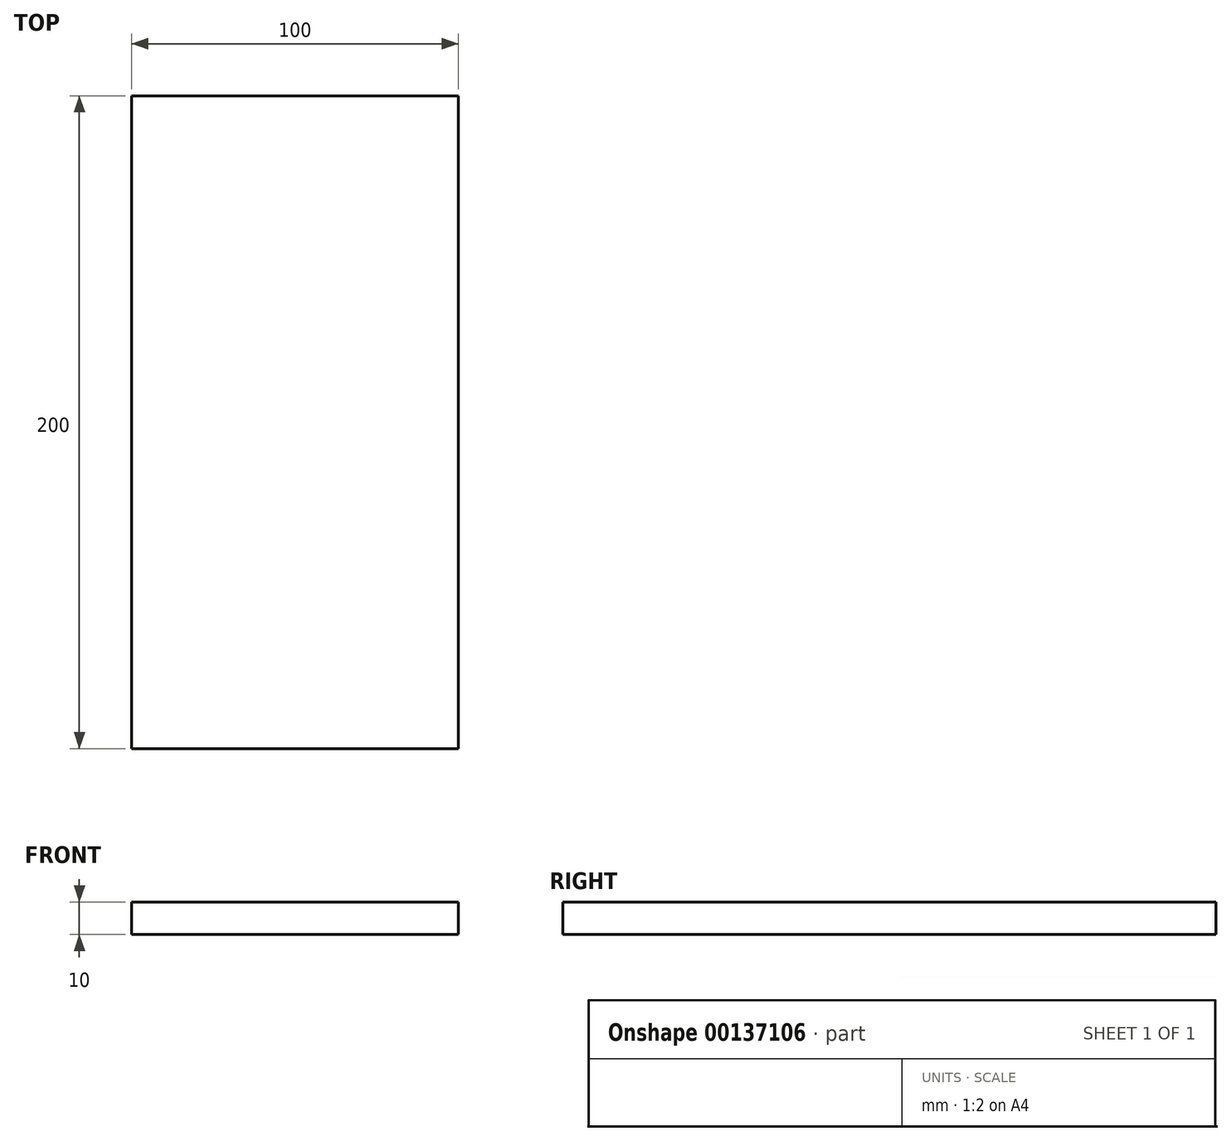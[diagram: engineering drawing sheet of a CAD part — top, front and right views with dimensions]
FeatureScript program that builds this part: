
annotation { "Feature Type Name" : "Feature", "Feature Type Description" : "" }
export const myFeature = defineFeature(function(context is Context, id is Id, definition is map)
    precondition{}
    {
        {
            var Q0;
            Q0=qCreatedBy(makeId("Top.planeOp"),FACE);
            var sketch = newSketch(context, id + "F0", { "sketchPlane" : qUnion([Q0])});
            skLineSegment(sketch, "E0.bottom", {"start": v(-39.16, 125.46) * mm, "end": v(60.84, 125.46) * mm});
            skLineSegment(sketch, "E0.top", {"start": v(-39.16, -74.54) * mm, "end": v(60.84, -74.54) * mm});
            skLineSegment(sketch, "E0.left", {"start": v(-39.16, 125.46) * mm, "end": v(-39.16, -74.54) * mm});
            skLineSegment(sketch, "E0.right", {"start": v(60.84, 125.46) * mm, "end": v(60.84, -74.54) * mm});
            skSolve(sketch);
        }
        {
            var Q0;
            Q0=makeQuery(id+"F0.imprint","IMPRINT",FACE,{"disambiguationData":[TD([[makeQuery(id+"F0.imprint","IMPRINT",EDGE,{"derivedFrom":sQuery(id+"F0.wireOp",EDGE,"E0.bottom")}),-1.0]])]});
            extrude(context, id + "F1", {"entities" : qUnion([Q0]), "depth" : 10 * mm});
        }
    });
